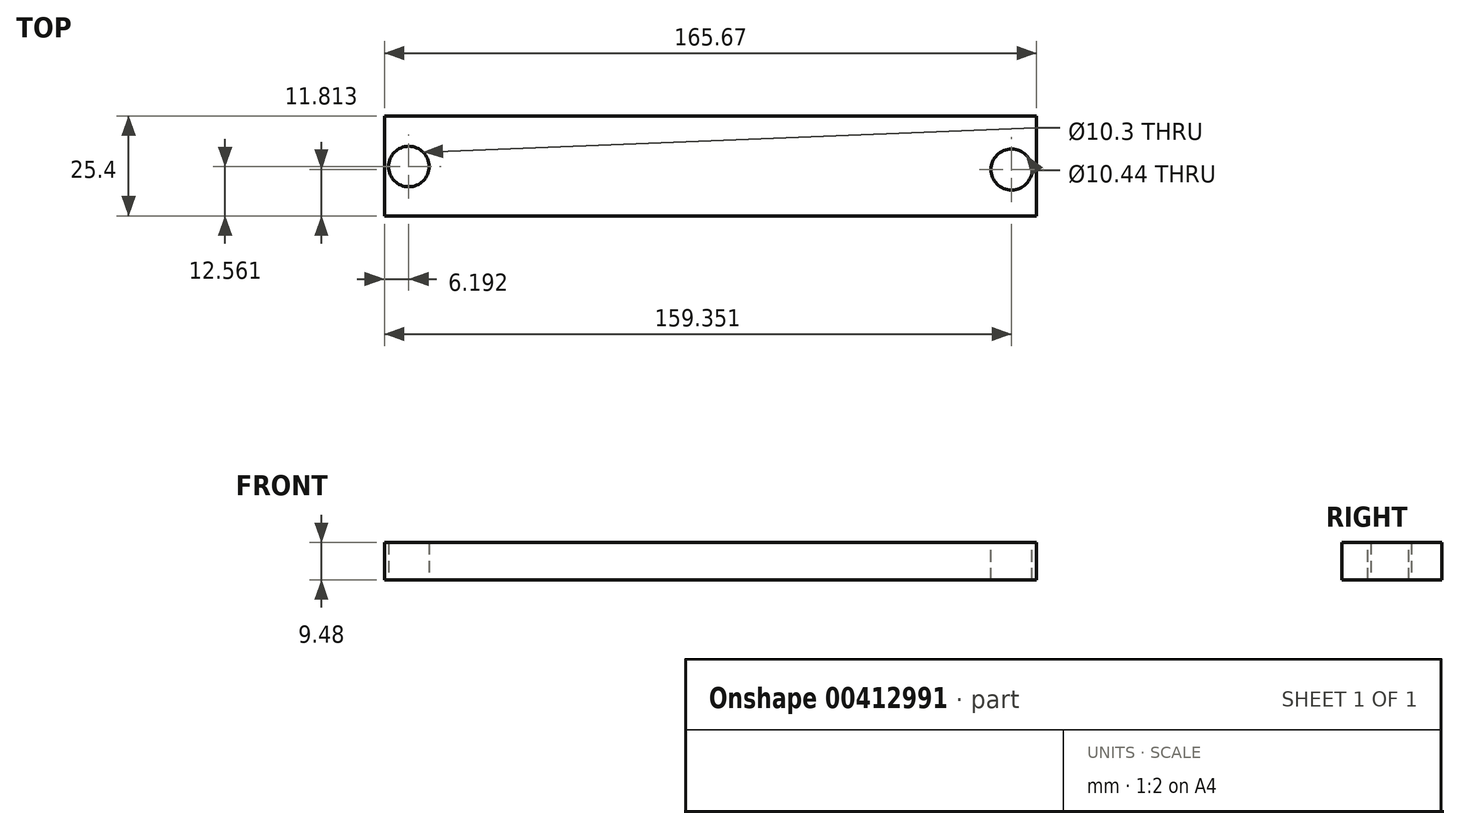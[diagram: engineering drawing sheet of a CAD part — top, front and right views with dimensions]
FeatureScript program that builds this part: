
annotation { "Feature Type Name" : "Feature", "Feature Type Description" : "" }
export const myFeature = defineFeature(function(context is Context, id is Id, definition is map)
    precondition{}
    {
        {
            var Q0;
            Q0=qCreatedBy(makeId("Front.planeOp"),FACE);
            var sketch = newSketch(context, id + "F0", { "sketchPlane" : qUnion([Q0])});
            skLineSegment(sketch, "E0.bottom", {"start": v(-30.53, 14.4) * mm, "end": v(135.14, 14.4) * mm});
            skLineSegment(sketch, "E0.top", {"start": v(-30.53, 4.93) * mm, "end": v(135.14, 4.93) * mm});
            skLineSegment(sketch, "E0.left", {"start": v(-30.53, 14.4) * mm, "end": v(-30.53, 4.93) * mm});
            skLineSegment(sketch, "E0.right", {"start": v(135.14, 14.4) * mm, "end": v(135.14, 4.93) * mm});
            skSolve(sketch);
        }
        {
            var Q0;
            Q0=makeQuery(id+"F0.imprint","IMPRINT",FACE,{"disambiguationData":[TD([[makeQuery(id+"F0.imprint","IMPRINT",EDGE,{"derivedFrom":sQuery(id+"F0.wireOp",EDGE,"E0.bottom")}),-1.0]])]});
            extrude(context, id + "F1", {"entities" : qUnion([Q0]), "depth" : 25.4 * mm});
        }
        {
            var Q0;
            Q0=makeQuery(id+"F1.opExtrude","SWEPT_FACE",FACE,{"disambiguationData":[OSD([sQuery(id+"F0.wireOp",EDGE,"E0.top")])]});
            var sketch = newSketch(context, id + "F2", { "sketchPlane" : qUnion([Q0])});
            skCircle(sketch, "E1", {"center": v(-24.34, 12.84) * mm, "radius": 5.15 * mm});
            skSolve(sketch);
        }
        {
            var Q0;
            Q0=makeQuery(id+"F2.imprint","IMPRINT",FACE,{"disambiguationData":[TD([[makeQuery(id+"F2.imprint","IMPRINT",EDGE,{"derivedFrom":sQuery(id+"F2.wireOp",EDGE,"E1")}),1.0]])]});
            extrude(context, id + "F3", {"entities" : qUnion([Q0]), "operationType" : NewBodyOperationType.REMOVE, "oppositeDirection" : true, "depth" : 25.4 * mm});
        }
        {
            var Q0;
            Q0=makeQuery(id+"F1.opExtrude","SWEPT_FACE",FACE,{"disambiguationData":[OSD([sQuery(id+"F0.wireOp",EDGE,"E0.bottom")])]});
            var sketch = newSketch(context, id + "F4", { "sketchPlane" : qUnion([Q0])});
            skCircle(sketch, "E2", {"center": v(128.82, -13.59) * mm, "radius": 5.22 * mm});
            skSolve(sketch);
        }
        {
            var Q0;
            Q0=makeQuery(id+"F4.imprint","IMPRINT",FACE,{"disambiguationData":[TD([[makeQuery(id+"F4.imprint","IMPRINT",EDGE,{"derivedFrom":sQuery(id+"F4.wireOp",EDGE,"E2")}),1.0]])]});
            extrude(context, id + "F5", {"entities" : qUnion([Q0]), "operationType" : NewBodyOperationType.REMOVE, "oppositeDirection" : true, "depth" : 25.4 * mm});
        }
    });
